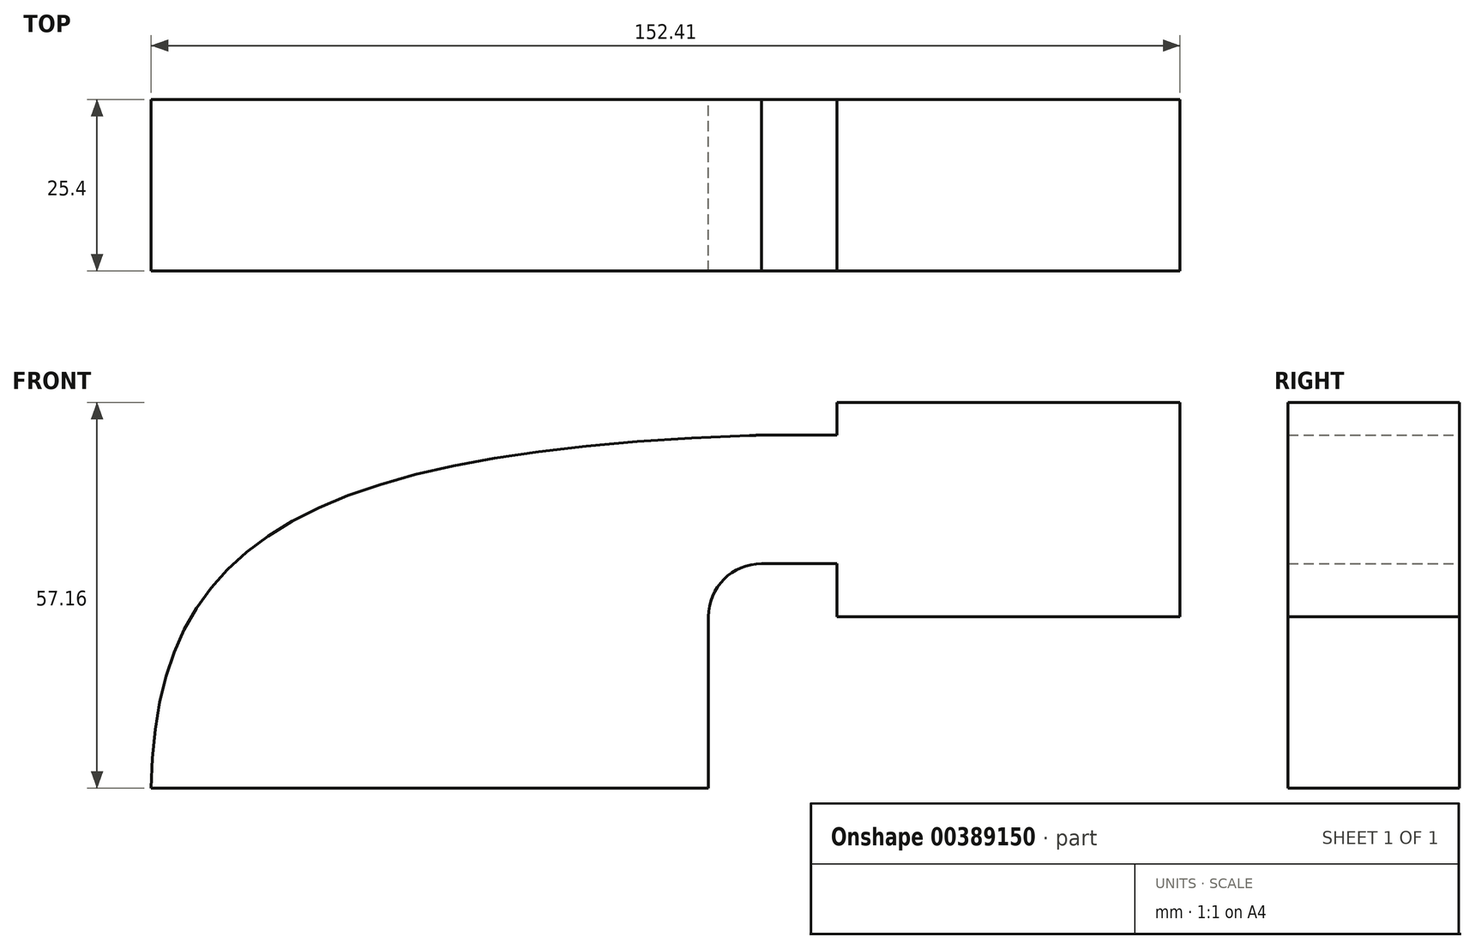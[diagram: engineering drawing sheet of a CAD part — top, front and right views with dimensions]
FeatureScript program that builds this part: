
annotation { "Feature Type Name" : "Feature", "Feature Type Description" : "" }
export const myFeature = defineFeature(function(context is Context, id is Id, definition is map)
    precondition{}
    {
        {
            var Q0;
            Q0=qCreatedBy(makeId("Front.planeOp"),FACE);
            var sketch = newSketch(context, id + "F0", { "sketchPlane" : qUnion([Q0])});
            skLineSegment(sketch, "E0.bottom", {"start": v(41.28, 9.53) * mm, "end": v(-41.28, 9.52) * mm});
            skLineSegment(sketch, "E0.top", {"start": v(41.28, -9.52) * mm, "end": v(-41.28, -9.53) * mm});
            skLineSegment(sketch, "E0.left", {"start": v(41.27, 9.53) * mm, "end": v(41.28, -9.52) * mm});
            skLineSegment(sketch, "E0.right", {"start": v(-41.28, 9.52) * mm, "end": v(-41.28, -9.53) * mm});
            skPoint(sketch, "E0.middle", {"position": v(0, 0) * mm});
            skLineSegment(sketch, "E1.bottom", {"start": v(111.12, 34.93) * mm, "end": v(60.33, 34.92) * mm});
            skLineSegment(sketch, "E1.top", {"start": v(111.12, 66.68) * mm, "end": v(60.33, 66.68) * mm});
            skLineSegment(sketch, "E1.left", {"start": v(111.12, 34.93) * mm, "end": v(111.12, 66.68) * mm});
            skLineSegment(sketch, "E1.right", {"start": v(60.33, 34.93) * mm, "end": v(60.33, 66.68) * mm});
            skPoint(sketch, "E1.middle", {"position": v(85.73, 50.8) * mm});
            skLineSegment(sketch, "E2", {"start": v(41.28, 9.53) * mm, "end": v(41.28, 34.93) * mm});
            skArc(sketch, "E3", {"start": v(41.27, 34.93) * mm, "mid": v(43.58, 40.5) * mm, "end": v(49.15, 42.8) * mm});
            skLineSegment(sketch, "E4", {"start": v(49.15, 42.8) * mm, "end": v(85.73, 42.8) * mm});
            skPoint(sketch, "E4.endSnap0", {"position": v(85.73, 34.93) * mm});
            skLineSegment(sketch, "E5.0", {"start": v(49.15, 61.85) * mm, "end": v(85.73, 61.85) * mm});
            skArc(sketch, "E5.1", {"start": v(22.22, 34.93) * mm, "mid": v(30.11, 53.96) * mm, "end": v(49.15, 61.85) * mm});
            skLineSegment(sketch, "E5.2", {"start": v(22.22, 9.53) * mm, "end": v(22.22, 34.93) * mm});
            skLineSegment(sketch, "E6", {"start": v(85.73, 34.93) * mm, "end": v(85.73, 66.68) * mm});
            skFitSpline(sketch, "E7", {"points": [v(-41.28, 9.52) * mm, v(49.15, 61.85) * mm], "startDerivative": vector(1.42, 106.64) * mm, "endDerivative": vector(208, 6.47) * mm});
            skSolve(sketch);
        }
        {
            var Q0;
            {var subQ0=sQuery(id+"F0.wireOp",EDGE,"E7");var subQ1=sQuery(id+"F0.wireOp",EDGE,"E5.1");var subQ3=makeQuery(id+"F0.imprint","INTERSECT",VERTEX,{"derivedFrom":[subQ1,subQ0]});Q0=makeQuery(id+"F0.imprint","IMPRINT",FACE,{"disambiguationData":[TD([[makeQuery(id+"F0.imprint","IMPRINT",EDGE,{"disambiguationData":[TD([[subQ3,-1.0]])],"derivedFrom":subQ1}),-1.0]])]});}
            var Q1;
            {var subQ3=sQuery(id+"F0.wireOp",EDGE,"E5.2");Q1=makeQuery(id+"F0.imprint","IMPRINT",FACE,{"disambiguationData":[TD([[makeQuery(id+"F0.imprint","IMPRINT",EDGE,{"derivedFrom":subQ3}),1.0]])]});}
            var Q2;
            {var subQ0=sQuery(id+"F0.wireOp",EDGE,"E1.right");var subQ1=sQuery(id+"F0.wireOp",EDGE,"E1.bottom");var subQ2=makeQuery(id+"F0.imprint","INTERSECT",VERTEX,{"derivedFrom":[subQ1,subQ0]});Q2=makeQuery(id+"F0.imprint","IMPRINT",FACE,{"disambiguationData":[TD([[makeQuery(id+"F0.imprint","IMPRINT",EDGE,{"disambiguationData":[TD([[subQ2,1.0]])],"derivedFrom":subQ1}),-1.0]])]});}
            var Q3;
            {var subQ0=sQuery(id+"F0.wireOp",EDGE,"E1.right");var subQ1=sQuery(id+"F0.wireOp",EDGE,"E1.top");var subQ2=makeQuery(id+"F0.imprint","INTERSECT",VERTEX,{"derivedFrom":[subQ1,subQ0]});Q3=makeQuery(id+"F0.imprint","IMPRINT",FACE,{"disambiguationData":[TD([[makeQuery(id+"F0.imprint","IMPRINT",EDGE,{"disambiguationData":[TD([[subQ2,1.0]])],"derivedFrom":subQ1}),1.0]])]});}
            var Q4;
            {var subQ0=sQuery(id+"F0.wireOp",EDGE,"E1.left");Q4=makeQuery(id+"F0.imprint","IMPRINT",FACE,{"disambiguationData":[TD([[makeQuery(id+"F0.imprint","IMPRINT",EDGE,{"derivedFrom":subQ0}),1.0]])]});}
            var Q5;
            {var subQ1=sQuery(id+"F0.wireOp",EDGE,"E2");Q5=makeQuery(id+"F0.imprint","IMPRINT",FACE,{"disambiguationData":[TD([[makeQuery(id+"F0.imprint","IMPRINT",EDGE,{"derivedFrom":subQ1}),1.0]])]});}
            var Q6;
            {var subQ0=sQuery(id+"F0.wireOp",EDGE,"E4");var subQ1=sQuery(id+"F0.wireOp",EDGE,"E1.right");var subQ2=makeQuery(id+"F0.imprint","INTERSECT",VERTEX,{"derivedFrom":[subQ1,subQ0]});Q6=makeQuery(id+"F0.imprint","IMPRINT",FACE,{"disambiguationData":[TD([[makeQuery(id+"F0.imprint","IMPRINT",EDGE,{"disambiguationData":[TD([[subQ2,-1.0]])],"derivedFrom":subQ1}),-1.0]])]});}
            extrude(context, id + "F1", {"entities" : qUnion([Q0, Q1, Q2, Q3, Q4, Q5, Q6]), "depth" : 25.4 * mm});
        }
    });
